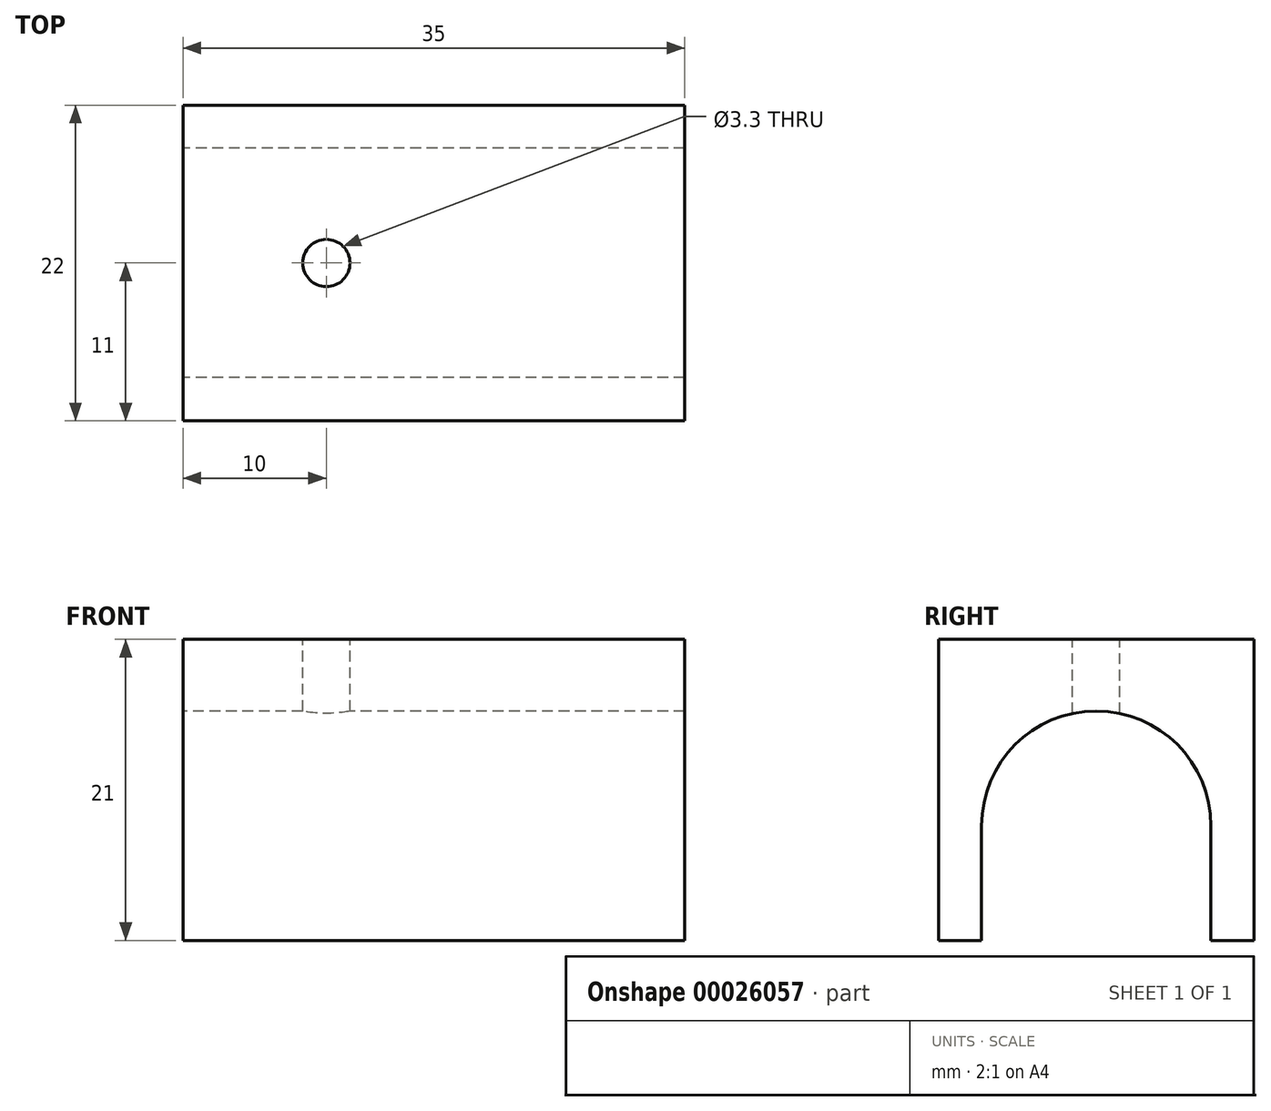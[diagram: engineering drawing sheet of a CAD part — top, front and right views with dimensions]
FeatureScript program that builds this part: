
annotation { "Feature Type Name" : "Feature", "Feature Type Description" : "" }
export const myFeature = defineFeature(function(context is Context, id is Id, definition is map)
    precondition{}
    {
        {
            var Q0;
            Q0=qCreatedBy(makeId("Right.planeOp"),FACE);
            var sketch = newSketch(context, id + "F0", { "sketchPlane" : qUnion([Q0])});
            skCircle(sketch, "E0", {"center": v(0, 8) * mm, "radius": 8 * mm, "construction": true});
            skLineSegment(sketch, "E1", {"start": v(-11, 0) * mm, "end": v(-11, 21) * mm});
            skLineSegment(sketch, "E2", {"start": v(-11, 21) * mm, "end": v(0, 21) * mm});
            skLineSegment(sketch, "E3", {"start": v(-11, 0) * mm, "end": v(-8, 0) * mm});
            skLineSegment(sketch, "E4", {"start": v(-8, 0) * mm, "end": v(-8, 8) * mm});
            skArc(sketch, "E5", {"start": v(-8, 8) * mm, "mid": v(-5.66, 13.66) * mm, "end": v(0, 16) * mm});
            skLineSegment(sketch, "E6.MirrorCS", {"start": v(11, 21) * mm, "end": v(0, 21) * mm});
            skLineSegment(sketch, "E7.MirrorCS", {"start": v(11, 0) * mm, "end": v(11, 21) * mm});
            skLineSegment(sketch, "E8.MirrorCS", {"start": v(11, 0) * mm, "end": v(8, 0) * mm});
            skLineSegment(sketch, "E9.MirrorCS", {"start": v(8, 0) * mm, "end": v(8, 8) * mm});
            skArc(sketch, "E10.MirrorCS", {"start": v(8, 8) * mm, "mid": v(5.66, 13.66) * mm, "end": v(0, 16) * mm});
            skSolve(sketch);
        }
        {
            var Q0;
            Q0 = qSketchRegion(id + "F0", true);
            extrude(context, id + "F1", {"entities" : qUnion([Q0]), "depth" : 35 * mm});
        }
        {
            var Q0;
            Q0=makeQuery(id+"F1.opExtrude","SWEPT_FACE",FACE,{"disambiguationData":[OSD([sQuery(id+"F0.wireOp",EDGE,"E2"),sQuery(id+"F0.wireOp",EDGE,"E6.MirrorCS")])]});
            var sketch = newSketch(context, id + "F2", { "sketchPlane" : qUnion([Q0])});
            skCircle(sketch, "E11", {"center": v(10, 0) * mm, "radius": 1.65 * mm});
            skSolve(sketch);
        }
        {
            var Q0;
            Q0 = qSketchRegion(id + "F2", true);
            extrude(context, id + "F3", {"entities" : qUnion([Q0]), "operationType" : NewBodyOperationType.REMOVE, "endBound" : BoundingType.THROUGH_ALL, "oppositeDirection" : true, "depth" : 25 * mm});
        }
    });
